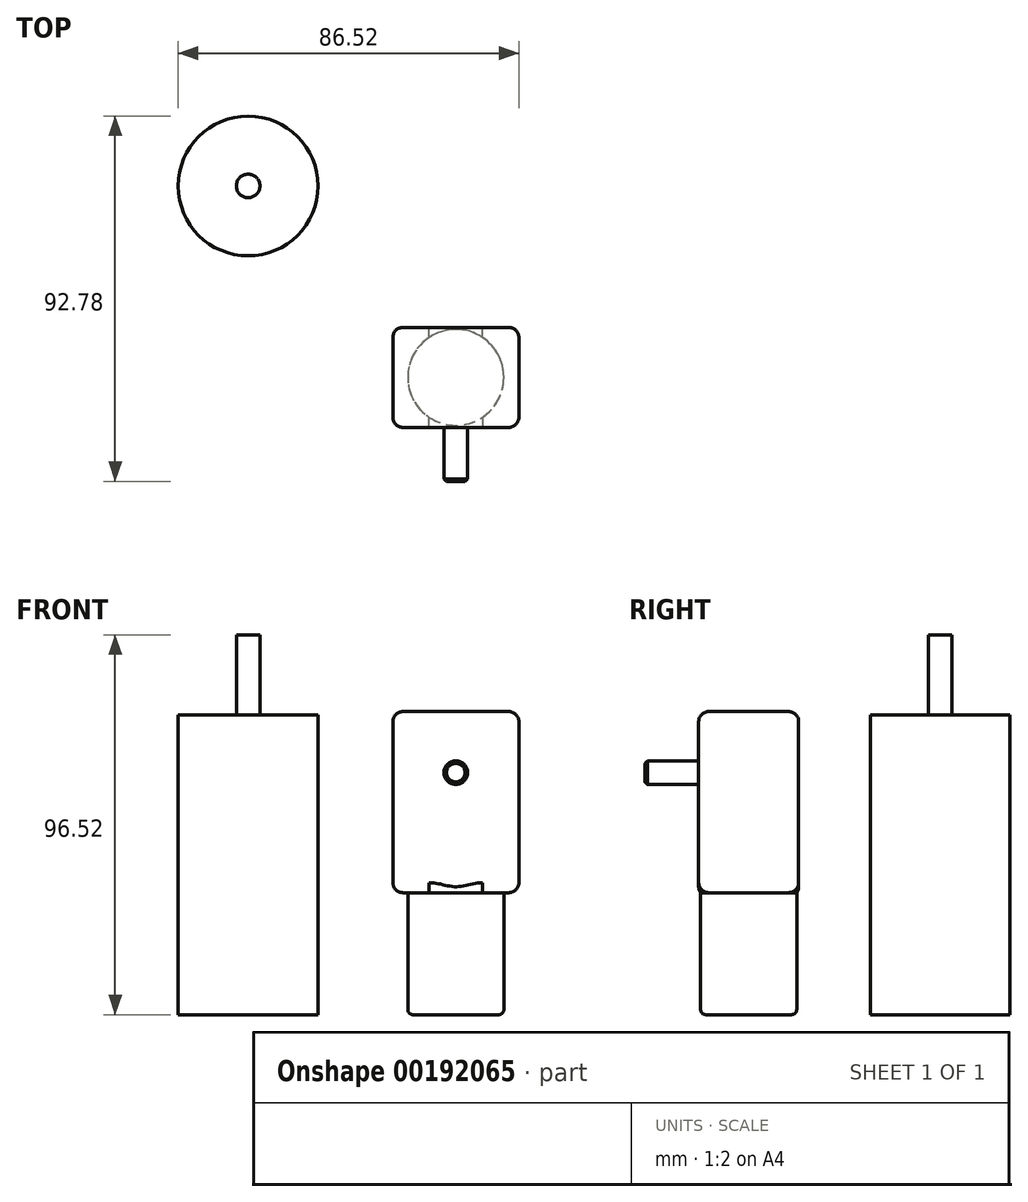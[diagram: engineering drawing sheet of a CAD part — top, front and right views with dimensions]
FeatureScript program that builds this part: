
annotation { "Feature Type Name" : "Feature", "Feature Type Description" : "" }
export const myFeature = defineFeature(function(context is Context, id is Id, definition is map)
    precondition{}
    {
        {
            var Q0;
            Q0=qCreatedBy(makeId("Top.planeOp"),FACE);
            var sketch = newSketch(context, id + "F0", { "sketchPlane" : qUnion([Q0])});
            skCircle(sketch, "E0", {"center": v(0, 0) * mm, "radius": 12.2 * mm});
            skSolve(sketch);
        }
        {
            var Q0;
            Q0=makeQuery(id+"F0.imprint","IMPRINT",FACE,{"disambiguationData":[TD([[makeQuery(id+"F0.imprint","IMPRINT",EDGE,{"derivedFrom":sQuery(id+"F0.wireOp",EDGE,"E0")}),1.0]])]});
            extrude(context, id + "F1", {"entities" : qUnion([Q0]), "depth" : 31 * mm});
        }
        {
            var Q0;
            Q0=makeQuery(id+"F1.opExtrude","CAP_FACE",FACE,{"disambiguationData":[OSD([sQuery(id+"F0.wireOp",EDGE,"E0")])],"isStart":false});
            var sketch = newSketch(context, id + "F2", { "sketchPlane" : qUnion([Q0])});
            skLineSegment(sketch, "E1.bottom", {"start": v(16, -12.7) * mm, "end": v(-16, -12.7) * mm});
            skLineSegment(sketch, "E1.top", {"start": v(16, 12.7) * mm, "end": v(-16, 12.7) * mm});
            skLineSegment(sketch, "E1.left", {"start": v(16, -12.7) * mm, "end": v(16, 12.7) * mm});
            skLineSegment(sketch, "E1.right", {"start": v(-16, -12.7) * mm, "end": v(-16, 12.7) * mm});
            skPoint(sketch, "E1.middle", {"position": v(0, 0) * mm});
            skSolve(sketch);
        }
        {
            var Q0;
            Q0=makeQuery(id+"F2.imprint","IMPRINT",FACE,{"disambiguationData":[TD([[makeQuery(id+"F2.imprint","IMPRINT",EDGE,{"derivedFrom":sQuery(id+"F2.wireOp",EDGE,"E1.bottom")}),-1.0]])]});
            var Q1;
            Q1=makeQuery(id+"F2.imprint","IMPRINT",FACE,{"disambiguationData":[TD([[makeQuery(id+"F2.imprint","IMPRINT",EDGE,{"derivedFrom":makeQuery(id+"F1.opExtrude","CAP_EDGE",EDGE,{"disambiguationData":[OSD([sQuery(id+"F0.wireOp",EDGE,"E0")])],"isStart":false})}),1.0]])]});
            extrude(context, id + "F3", {"entities" : qUnion([Q0, Q1]), "operationType" : NewBodyOperationType.ADD, "depth" : 46 * mm});
        }
        {
            var Q0;
            Q0=makeQuery(id+"F3.opExtrude","SWEPT_FACE",FACE,{"disambiguationData":[OSD([sQuery(id+"F2.wireOp",EDGE,"E1.bottom")])]});
            var sketch = newSketch(context, id + "F4", { "sketchPlane" : qUnion([Q0])});
            skCircle(sketch, "E2", {"center": v(0, 61.5) * mm, "radius": 3 * mm});
            skSolve(sketch);
        }
        {
            var Q0;
            Q0=makeQuery(id+"F4.imprint","IMPRINT",FACE,{"disambiguationData":[TD([[makeQuery(id+"F4.imprint","IMPRINT",EDGE,{"derivedFrom":sQuery(id+"F4.wireOp",EDGE,"E2")}),1.0]])]});
            extrude(context, id + "F5", {"entities" : qUnion([Q0]), "operationType" : NewBodyOperationType.ADD, "depth" : 13.7 * mm});
        }
        {
            var Q0;
            Q0=makeQuery(id+"F3.opExtrude","SWEPT_EDGE",EDGE,{"disambiguationData":[OSD([sQuery(id+"F2.wireOp",EDGE,"E1.bottom"),sQuery(id+"F2.wireOp",EDGE,"E1.left")])]});
            var Q1;
            Q1=makeQuery(id+"F3.opExtrude","SWEPT_EDGE",EDGE,{"disambiguationData":[OSD([sQuery(id+"F2.wireOp",EDGE,"E1.top"),sQuery(id+"F2.wireOp",EDGE,"E1.left")])]});
            var Q2;
            Q2=makeQuery(id+"F3.opExtrude","CAP_EDGE",EDGE,{"disambiguationData":[OSD([sQuery(id+"F2.wireOp",EDGE,"E1.left")])],"isStart":true});
            var Q3;
            Q3=makeQuery(id+"F3.opExtrude","CAP_EDGE",EDGE,{"disambiguationData":[OSD([sQuery(id+"F2.wireOp",EDGE,"E1.left")])],"isStart":false});
            var Q4;
            Q4=makeQuery(id+"F3.opExtrude","CAP_EDGE",EDGE,{"disambiguationData":[OSD([sQuery(id+"F2.wireOp",EDGE,"E1.bottom")])],"isStart":false});
            var Q5;
            Q5=makeQuery(id+"F3.opExtrude","CAP_EDGE",EDGE,{"disambiguationData":[OSD([sQuery(id+"F2.wireOp",EDGE,"E1.top")])],"isStart":false});
            var Q6;
            Q6=makeQuery(id+"F3.opExtrude","CAP_EDGE",EDGE,{"disambiguationData":[OSD([sQuery(id+"F2.wireOp",EDGE,"E1.right")])],"isStart":false});
            var Q7;
            Q7=makeQuery(id+"F3.opExtrude","SWEPT_EDGE",EDGE,{"disambiguationData":[OSD([sQuery(id+"F2.wireOp",EDGE,"E1.top"),sQuery(id+"F2.wireOp",EDGE,"E1.right")])]});
            var Q8;
            Q8=makeQuery(id+"F3.opExtrude","SWEPT_EDGE",EDGE,{"disambiguationData":[OSD([sQuery(id+"F2.wireOp",EDGE,"E1.bottom"),sQuery(id+"F2.wireOp",EDGE,"E1.right")])]});
            var Q9;
            Q9=makeQuery(id+"F3.opExtrude","CAP_EDGE",EDGE,{"disambiguationData":[OSD([sQuery(id+"F2.wireOp",EDGE,"E1.bottom")])],"isStart":true});
            var Q10;
            Q10=makeQuery(id+"F3.opExtrude","CAP_EDGE",EDGE,{"disambiguationData":[OSD([sQuery(id+"F2.wireOp",EDGE,"E1.right")])],"isStart":true});
            var Q11;
            Q11=makeQuery(id+"F3.opExtrude","CAP_EDGE",EDGE,{"disambiguationData":[OSD([sQuery(id+"F2.wireOp",EDGE,"E1.top")])],"isStart":true});
            fillet(context, id + "F6", {"entities" : qUnion([Q0, Q1, Q2, Q3, Q4, Q5, Q6, Q7, Q8, Q9, Q10, Q11]), "radius" : 2.54 * mm, "tangentPropagation" : true, "allowEdgeOverflow" : false});
        }
        {
            var Q0;
            Q0=makeQuery(id+"F1.opExtrude","CAP_EDGE",EDGE,{"disambiguationData":[OSD([sQuery(id+"F0.wireOp",EDGE,"E0")])],"isStart":true});
            fillet(context, id + "F7", {"entities" : qUnion([Q0]), "radius" : 1.27 * mm, "tangentPropagation" : true, "allowEdgeOverflow" : false});
        }
        {
            var Q0;
            Q0=makeQuery(id+"F5.opExtrude","CAP_EDGE",EDGE,{"disambiguationData":[OSD([sQuery(id+"F4.wireOp",EDGE,"E2")])],"isStart":false});
            chamfer(context, id + "F8", {"entities" : qUnion([Q0]), "width" : 0.64 * mm, "tangentPropagation" : true});
        }
        {
            var Q0;
            Q0=qCreatedBy(makeId("Top.planeOp"),FACE);
            var sketch = newSketch(context, id + "F9", { "sketchPlane" : qUnion([Q0])});
            skCircle(sketch, "E3", {"center": v(-52.77, 48.63) * mm, "radius": 17.75 * mm});
            skSolve(sketch);
        }
        {
            var Q0;
            Q0=makeQuery(id+"F9.imprint","IMPRINT",FACE,{"disambiguationData":[TD([[makeQuery(id+"F9.imprint","IMPRINT",EDGE,{"derivedFrom":sQuery(id+"F9.wireOp",EDGE,"E3")}),1.0]])]});
            extrude(context, id + "F10", {"entities" : qUnion([Q0]), "depth" : 76.2 * mm});
        }
        {
            var Q0;
            Q0=makeQuery(id+"F10.opExtrude","CAP_FACE",FACE,{"disambiguationData":[OSD([sQuery(id+"F9.wireOp",EDGE,"E3")])],"isStart":false});
            var sketch = newSketch(context, id + "F11", { "sketchPlane" : qUnion([Q0])});
            skCircle(sketch, "E4", {"center": v(-52.77, 48.63) * mm, "radius": 3 * mm});
            skSolve(sketch);
        }
        {
            var Q0;
            Q0=makeQuery(id+"F11.imprint","IMPRINT",FACE,{"disambiguationData":[TD([[makeQuery(id+"F11.imprint","IMPRINT",EDGE,{"derivedFrom":sQuery(id+"F11.wireOp",EDGE,"E4")}),1.0]])]});
            var Q1;
            Q1=sQuery(id+"F11.wireOp",EDGE,"E4");
            extrude(context, id + "F12", {"entities" : qUnion([Q0]), "operationType" : NewBodyOperationType.ADD, "surfaceEntities" : qUnion([Q1]), "depth" : 20.32 * mm});
        }
    });
